# Revit family: Ayla Barstool Option 2
name_source: partatom
category: Furniture
revit_build: Autodesk Revit 2017 (Build: 20160225_1515(x64)
units: mm (PartAtom-declared; Revit-internal decimal feet)

## family parameters
Always vertical = Yes
Cut with Voids When Loaded = No
OmniClass Number = 23.40.20.00
OmniClass Title = General Furniture and Specialties
Room Calculation Point = No
Shared = No
Work Plane-Based = No

## types (1)
- Ayla Barstool Option 2
    Assembly Code = E2020200
    Assistance = Call for assistance number: 336.941.3446
    Back material = Standard wood finishes or Cof
    Barstool type = 4-Leg
    Collection = Ayla
    Depth = 20 mm  [stored 0.0656168 ft]
    Description = Barstool with metal frame, upholstered seat and upholstered on front and stained wood back
    Height = 39 mm  [stored 0.127953 ft]
    Industry = Café, Restaurant, Bistro, Hotel, Club, College
    Length = 19 mm  [stored 0.062336 ft]
    Manufacturer = Beaufurn
    Manufacturer Country = USA
    Model = Ayla Barstool Option 2
    Products of collection = Ayla Chairs
    Seat height = 30 mm  [stored 0.0984252 ft]
    Structure material = Steel
    Type Comments = Perfect for cafés, restaurants, and other venues
    URL = http://beaufurn.com
    Upholstery material = Graded Fabric or Com
    Usage = Indoor

note: [stored X ft] marks values corroborated as IEEE doubles in the binary element streams (Revit-internal decimal feet)

## geometry (parser evidence)
native form markers: Sweep x3
no freeform markers — native parametric forms only
